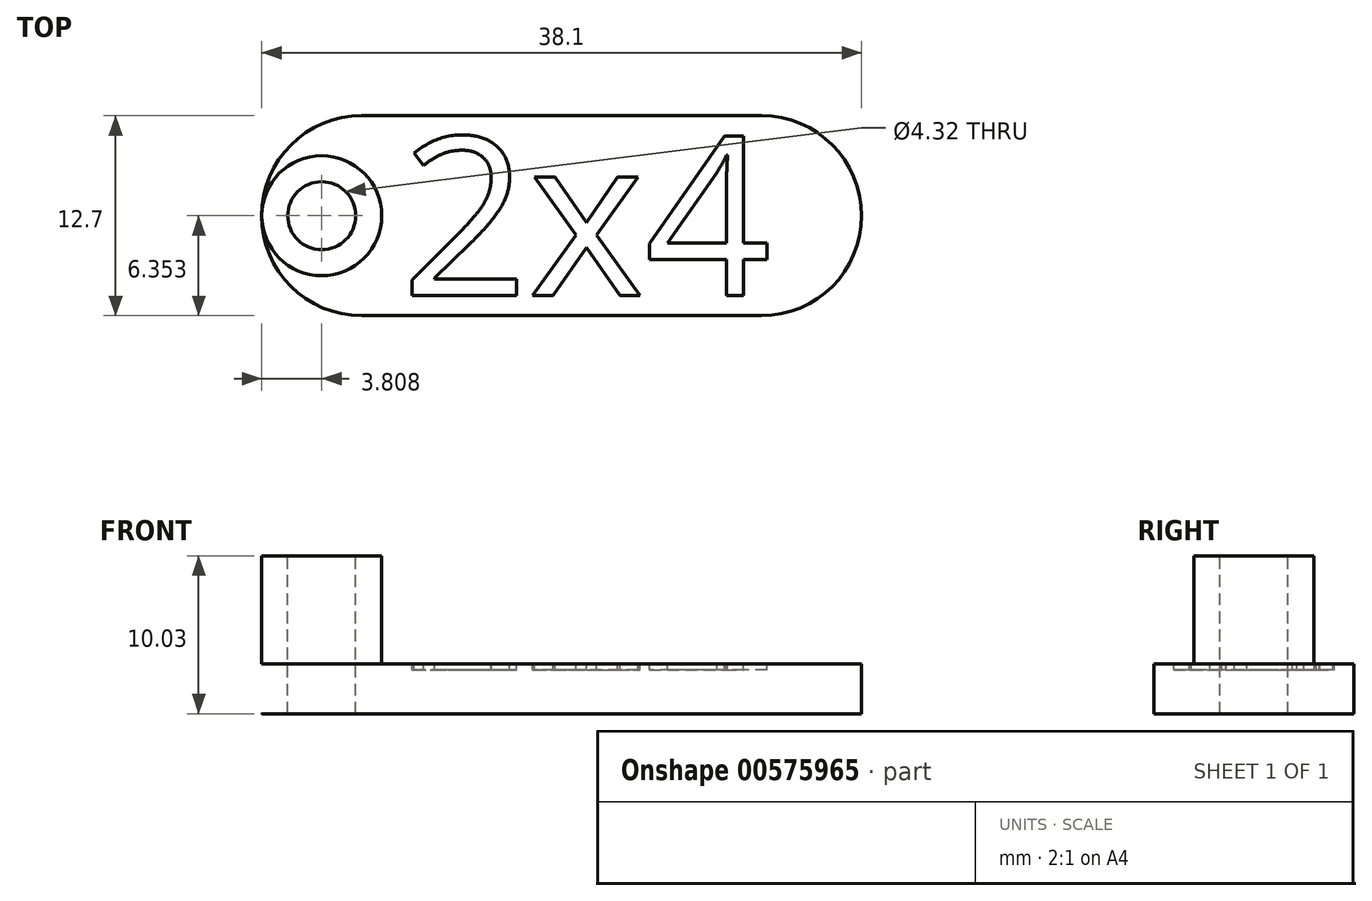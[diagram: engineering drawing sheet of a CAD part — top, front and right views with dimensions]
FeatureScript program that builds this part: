
annotation { "Feature Type Name" : "Feature", "Feature Type Description" : "" }
export const myFeature = defineFeature(function(context is Context, id is Id, definition is map)
    precondition{}
    {
        {
            var Q0;
            Q0=qCreatedBy(makeId("Top.planeOp"),FACE);
            var sketch = newSketch(context, id + "F0", { "sketchPlane" : qUnion([Q0])});
            skLineSegment(sketch, "E0.bottom", {"start": v(-47.46, -10.56) * mm, "end": v(-9.36, -10.56) * mm});
            skLineSegment(sketch, "E0.top", {"start": v(-47.46, -23.26) * mm, "end": v(-9.36, -23.26) * mm});
            skLineSegment(sketch, "E0.left", {"start": v(-47.46, -10.56) * mm, "end": v(-47.46, -23.26) * mm});
            skLineSegment(sketch, "E0.right", {"start": v(-9.36, -10.56) * mm, "end": v(-9.36, -23.26) * mm});
            skSolve(sketch);
        }
        {
            var Q0;
            Q0=qSketchRegion(id+"F0",true);
            extrude(context, id + "F1", {"entities" : qUnion([Q0]), "depth" : 3.17 * mm, "offsetDistance" : 25.4 * mm, "flatOperationType" : FlatOperationType.REMOVE, "domain" : OperationDomain.MODEL});
        }
        {
            var Q0;
            Q0=makeQuery(id+"F1.opExtrude","CAP_FACE",FACE,{"disambiguationData":[OSD([sQuery(id+"F0.wireOp",EDGE,"E0.bottom"),sQuery(id+"F0.wireOp",EDGE,"E0.top"),sQuery(id+"F0.wireOp",EDGE,"E0.left"),sQuery(id+"F0.wireOp",EDGE,"E0.right")])],"isStart":false});
            var sketch = newSketch(context, id + "F2", { "sketchPlane" : qUnion([Q0])});
            skCircle(sketch, "E1", {"center": v(-43.65, -16.9) * mm, "radius": 3.81 * mm});
            skPoint(sketch, "E1.centerSnap0", {"position": v(-47.46, -16.9) * mm});
            skSolve(sketch);
        }
        {
            var Q0;
            Q0=makeQuery(id+"F2.imprint","IMPRINT",FACE,{"disambiguationData":[TD([[makeQuery(id+"F2.imprint","IMPRINT",EDGE,{"derivedFrom":sQuery(id+"F2.wireOp",EDGE,"E1")}),1.0]])]});
            extrude(context, id + "F3", {"entities" : qUnion([Q0]), "operationType" : NewBodyOperationType.ADD, "depth" : 6.86 * mm, "offsetDistance" : 25.4 * mm, "flatOperationType" : FlatOperationType.REMOVE, "domain" : OperationDomain.MODEL});
        }
        {
            var Q0;
            Q0=makeQuery(id+"F3.opExtrude","CAP_FACE",FACE,{"disambiguationData":[OSD([sQuery(id+"F2.wireOp",EDGE,"E1")])],"isStart":false});
            var sketch = newSketch(context, id + "F4", { "sketchPlane" : qUnion([Q0])});
            skCircle(sketch, "E2", {"center": v(-43.65, -16.9) * mm, "radius": 2.16 * mm});
            skSolve(sketch);
        }
        {
            var Q0;
            Q0=qSketchRegion(id+"F4",true);
            extrude(context, id + "F5", {"entities" : qUnion([Q0]), "operationType" : NewBodyOperationType.REMOVE, "oppositeDirection" : true, "depth" : 25.4 * mm, "offsetDistance" : 25.4 * mm});
        }
        {
            var Q0;
            Q0=makeQuery(id+"F1.opExtrude","SWEPT_EDGE",EDGE,{"disambiguationData":[OSD([sQuery(id+"F0.wireOp",EDGE,"E0.bottom"),sQuery(id+"F0.wireOp",EDGE,"E0.left")])]});
            var Q1;
            Q1=makeQuery(id+"F1.opExtrude","SWEPT_EDGE",EDGE,{"disambiguationData":[OSD([sQuery(id+"F0.wireOp",EDGE,"E0.top"),sQuery(id+"F0.wireOp",EDGE,"E0.left")])]});
            var Q2;
            Q2=makeQuery(id+"F1.opExtrude","SWEPT_EDGE",EDGE,{"disambiguationData":[OSD([sQuery(id+"F0.wireOp",EDGE,"E0.bottom"),sQuery(id+"F0.wireOp",EDGE,"E0.right")])]});
            var Q3;
            Q3=makeQuery(id+"F1.opExtrude","SWEPT_EDGE",EDGE,{"disambiguationData":[OSD([sQuery(id+"F0.wireOp",EDGE,"E0.top"),sQuery(id+"F0.wireOp",EDGE,"E0.right")])]});
            fillet(context, id + "F6", {"entities" : qUnion([Q0, Q1, Q2, Q3]), "radius" : 6.35 * mm, "tangentPropagation" : true, "allowEdgeOverflow" : false});
        }
        {
            var Q0;
            Q0=makeQuery(id+"F1.opExtrude","CAP_FACE",FACE,{"disambiguationData":[OSD([sQuery(id+"F0.wireOp",EDGE,"E0.bottom"),sQuery(id+"F0.wireOp",EDGE,"E0.top"),sQuery(id+"F0.wireOp",EDGE,"E0.left"),sQuery(id+"F0.wireOp",EDGE,"E0.right")])],"isStart":false});
            var sketch = newSketch(context, id + "F7", { "sketchPlane" : qUnion([Q0])});
            skText(sketch, "E3", { "text": "2x4", "fontName": "OpenSans-Regular.ttf"});
            const initialGuessF7  = {"E3": [-0.0386, -0.02199, 1, 0, 0.01016]};
            skSetInitialGuess(sketch, initialGuessF7);
            skSolve(sketch);
        }
        {
            var Q0;
            Q0 = qSketchRegion(id + "F7", true);
            extrude(context, id + "F8", {"entities" : qUnion([Q0]), "operationType" : NewBodyOperationType.REMOVE, "oppositeDirection" : true, "depth" : 0.38 * mm, "offsetDistance" : 25.4 * mm});
        }
    });
